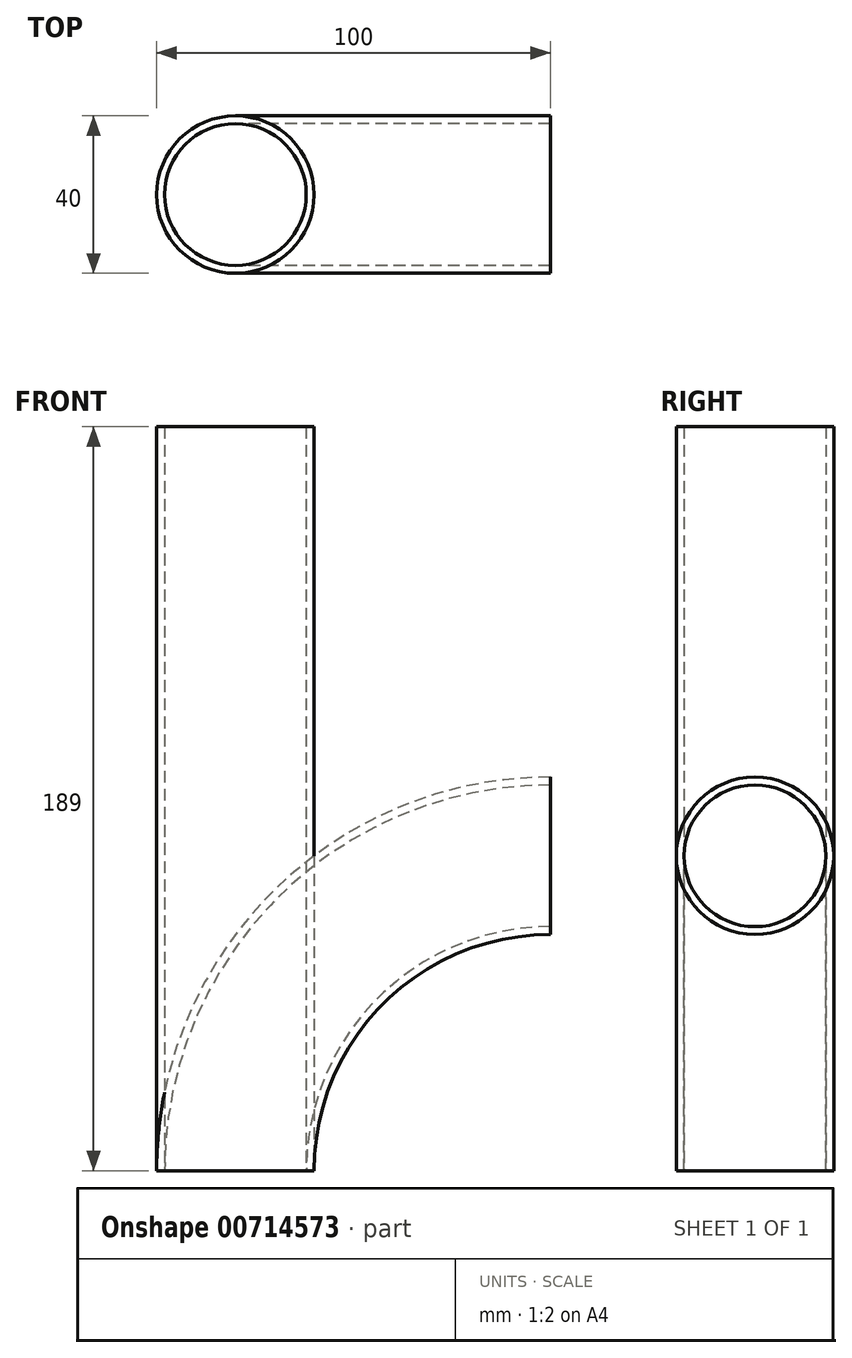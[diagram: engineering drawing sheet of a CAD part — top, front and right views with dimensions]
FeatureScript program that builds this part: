
annotation { "Feature Type Name" : "Feature", "Feature Type Description" : "" }
export const myFeature = defineFeature(function(context is Context, id is Id, definition is map)
    precondition{}
    {
        {
            var Q0;
            Q0=qCreatedBy(makeId("Top.planeOp"),FACE);
            var sketch = newSketch(context, id + "F0", { "sketchPlane" : qUnion([Q0])});
            skCircle(sketch, "E0", {"center": v(0, 0) * mm, "radius": 20 * mm});
            skSolve(sketch);
        }
        {
            var Q0;
            Q0 = qSketchRegion(id + "F0", true);
            extrude(context, id + "F1", {"entities" : qUnion([Q0]), "depth" : 189 * mm, "offsetDistance" : 25 * mm});
        }
        {
            var Q0;
            Q0=qCreatedBy(makeId("Top.planeOp"),FACE);
            var sketch = newSketch(context, id + "F2", { "sketchPlane" : qUnion([Q0])});
            skLineSegment(sketch, "E1", {"start": v(80, 0) * mm, "end": v(80, 93.24) * mm, "construction": true});
            skSolve(sketch);
        }
        {
            var Q0;
            Q0=makeQuery(id+"F0.imprint","IMPRINT",FACE,{"disambiguationData":[TD([[makeQuery(id+"F0.imprint","IMPRINT",EDGE,{"derivedFrom":sQuery(id+"F0.wireOp",EDGE,"E0")}),1.0]])]});
            var Q1;
            Q1=sQuery(id+"F2.wireOp",EDGE,"E1");
            revolve(context, id + "F3", {"surfaceOperationType" : NewSurfaceOperationType.NEW, "entities" : qUnion([Q0]), "axis" : qUnion([Q1]), "revolveType" : RevolveType.ONE_DIRECTION, "angle" : 90 * degree});
        }
        {
            var Q0;
            Q0=makeQuery(id+"F3.opRevolve","CAP_FACE",FACE,{"disambiguationData":[OSD([sQuery(id+"F0.wireOp",EDGE,"E0")])],"isStart":false});
            var Q1;
            Q1=makeQuery(id+"F3.opRevolve","CAP_FACE",FACE,{"disambiguationData":[OSD([sQuery(id+"F0.wireOp",EDGE,"E0")])],"isStart":true});
            var Q2;
            Q2=makeQuery(id+"F1.opExtrude","CAP_FACE",FACE,{"disambiguationData":[OSD([sQuery(id+"F0.wireOp",EDGE,"E0")])],"isStart":true});
            var Q3;
            Q3=makeQuery(id+"F1.opExtrude","CAP_FACE",FACE,{"disambiguationData":[OSD([sQuery(id+"F0.wireOp",EDGE,"E0")])],"isStart":false});
            shell(context, id + "F4", {"entities" : qUnion([Q0, Q1, Q2, Q3]), "thickness" : 2 * mm});
        }
    });
